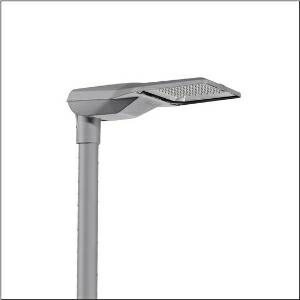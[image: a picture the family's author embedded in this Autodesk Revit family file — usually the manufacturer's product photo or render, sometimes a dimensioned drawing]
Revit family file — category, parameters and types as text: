
# Revit family: streetlight_sl_21_iq_midi___st0_5a_5xe3b31g08mb_2812
name_source: partatom
category: Lighting Fixtures
units: mm (PartAtom-declared; Revit-internal decimal feet)

## family parameters
Cut with Voids When Loaded = No
Host = Face
Light Source = No
Part Type = Normal
Room Calculation Point = No
Round Connector Dimension = Use Diameter
Shared = No

## types (1)
- --- (1 x LED, 19500 lm, 146.7 W, 3000K)
    Apparent Load = 147 VA
    CIE Flux Codes = 41 75 97 100 100
    Color Rendering = 70
    Color Temperature = 3000K
    Default Elevation = 1800 mm
    Description = Streetlight SL 21 iQ midi, mast luminaire, primary light control with lens, of PMMA, primary optical cover: cover, of toughened safety glass, transparent, light distribution: ST0.5a, light emission: direct distribution, primary light characteristic: asymmetric, installation type: post-top, side-entry, LED, High Power LED, rated luminous flux: 19.500lm, luminous efficacy: 133lm/W, light colour: 730, colour temperature: 3000K, control gear: iQ Street-Remote, control: Street-Remote, Auto-Match, Temp-Guard, Lumen-Switch, Night-Set, Smart-Wire, Light-Fading, Desk-Remote (wireless, voltage-free reading and setting of iQ features in the workshop via application-optimized NFC function/RFID function), optimised constant luminous flux control (CLO 2.0), pre-setting: linear dimming characteristic, mains connection: 230..240V, AC, 50/60Hz, start of lifetime: 147W, end of service life: 161W, reduction: 62W, luminaire housing, of diecast aluminium, powder-coated, SITECO metallic grey (DB 702S), corrosivity category C5 high according to DIN EN ISO 12944, please order mast flange separately, inclination adjustable: 0°, 5°, 10°, 15°, sealing non-destructively replaceable, multi-level sealing system, length: 644mm, width: 335mm, height: 110mm, mast flange for spigot size: 42mm (side-entry): 5XC10008XM4, 60/48mm (side-entry/post-top): 5XC10108XM2, 76/60mm (side-entry/post-top): 5XC10108XM1, mounting height: 4..8m, protection rating (complete): IP66, insulation class (complete): insulation class II (safety insulation), certification: CE, ENEC, ENEC+, VDE, impact resistance: IK10, permissible operating ambient temperature for outdoor applications: -40..+50°C, standard-compliant lighting for roads and squares, packaging unit: 1 piece

Light Distribution: ST0.5a
    Height = 111 mm
    Lamp = 1 x LED
    Lamp Light Flux = 19500 lm
    Lamp Power = 146.7 W
    Lamp count = 1
    Length = 644 mm
    Luminous efficacy = 133 lm/W
    Manufacturer = Siteco
    ModVariant = No
    Model = 5XE3B31G08MB
    Number of Poles = 1
    OnlyDefault = Yes
    Power Factor = 1
    Product Name = Streetlight SL 21 iQ midi | ST0.5a
    Product group = mast luminaire | pylon top
    ProductGroupID = 6100
    Protection Class = Protection class II
    Protection Degree = IP 66
    RLX_Detail_Level = 1
    RLX_Emergency_Light_Flux = 0 lm
    RLX_Emergency_Type = 0
    RLX_Emergency_Type_DB = No
    RlxData = <blob elided: 37865 chars, md5=b6ae55ad>
    Socket = socket
    Standby Power = 0 W
    System Light Flux = 19499 lm
    System Power = 147 W
    Type Comments = factory setting: luminous flux: 100 % | dim-lin: 254 | 753 mA
    Type Image = l_1004298.jpg
    URL = http://relux.com
    VarID = @adj_189299
    Voltage = 0 V
    Weight = 0.00 kg
    Width = 336 mm

## geometry (parser evidence)
native form markers: Blend x4, Sweep x8
no freeform markers — native parametric forms only
